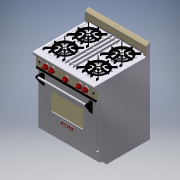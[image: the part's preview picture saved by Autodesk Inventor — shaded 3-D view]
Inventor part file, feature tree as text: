
AUTODESK INVENTOR PART (.ipt)
format: ipt  version: 2016 (Build 200138000, 138)  size: 20,678,144 bytes
history: native  units: in
note: dims shown in document units (in); Inventor stores cm internally (conversion verified against a paired STEP export)
features: fillet x5, imported_body x1
ambient origin geometry x8: Origin, YZ Plane, XZ Plane, XY Plane, X Axis, Y Axis, Z Axis, Center Point
bodies: Solid1 (feature_tree)
feature tree (6):
  imported_body  "Base1"
  fillet  "Fillet1"  Radius=0.0312in
  fillet  "Fillet2"  Radius=0.0312in
  fillet  "Fillet3"  Radius=0.0312in
  fillet  "Fillet4"  Radius=0.0312in
  fillet  "Fillet5"  Radius=0.0312in
